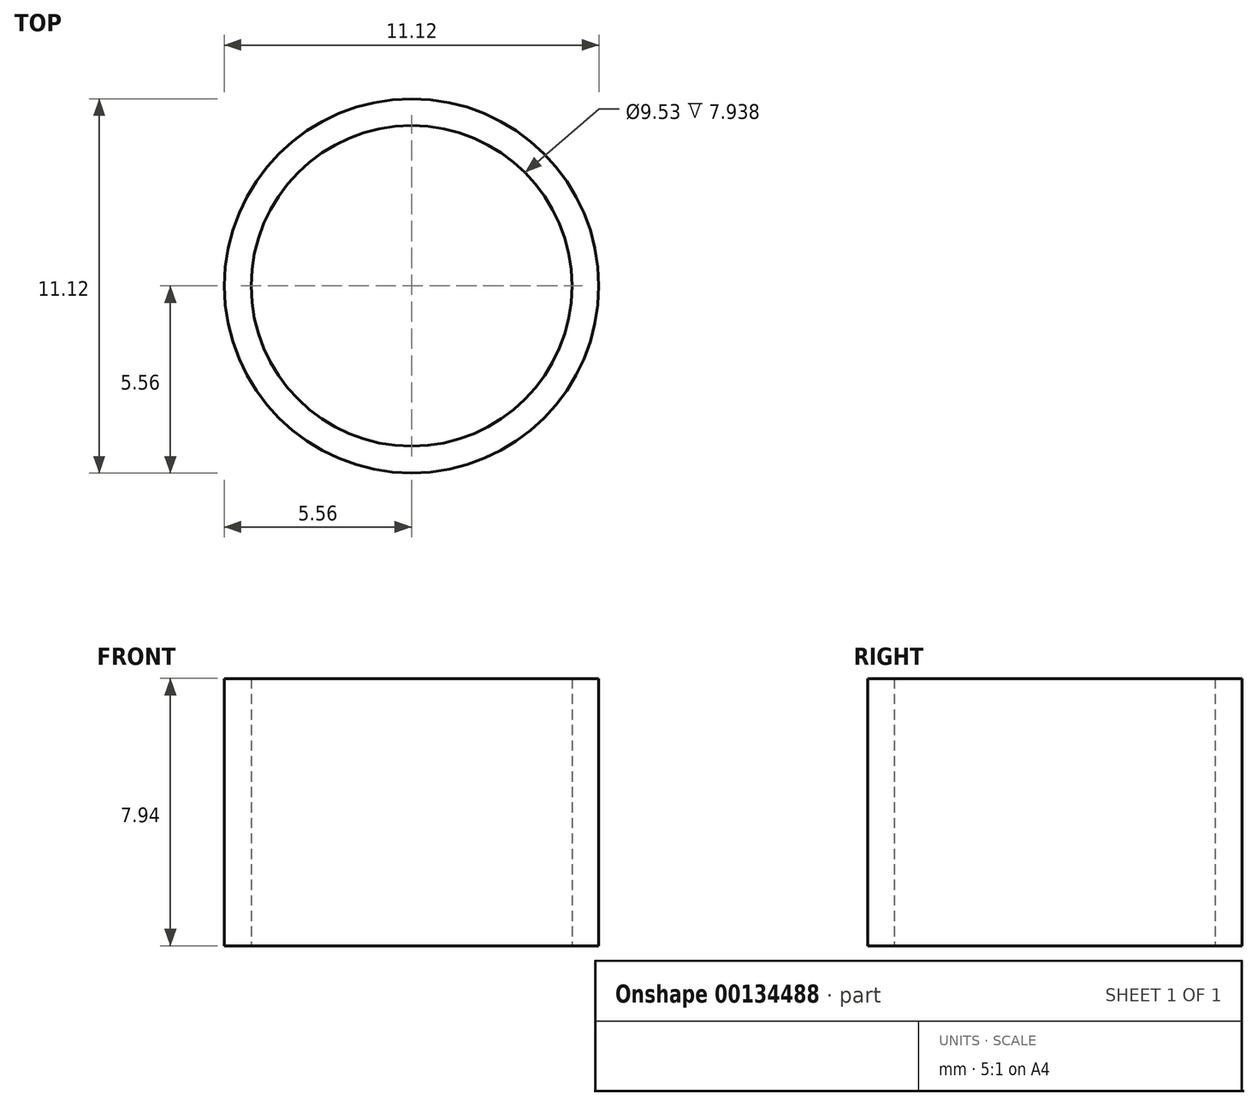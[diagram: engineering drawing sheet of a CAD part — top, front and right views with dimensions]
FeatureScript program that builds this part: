
annotation { "Feature Type Name" : "Feature", "Feature Type Description" : "" }
export const myFeature = defineFeature(function(context is Context, id is Id, definition is map)
    precondition{}
    {
        {
            var Q0;
            Q0=qCreatedBy(makeId("Top.planeOp"),FACE);
            var sketch = newSketch(context, id + "F0", { "sketchPlane" : qUnion([Q0])});
            skCircle(sketch, "E0", {"center": v(0, 0) * mm, "radius": 5.56 * mm});
            skCircle(sketch, "E1", {"center": v(0, 0) * mm, "radius": 4.76 * mm});
            skSolve(sketch);
        }
        {
            var Q0;
            Q0 = qSketchRegion(id + "F0", true);
            extrude(context, id + "F1", {"entities" : qUnion([Q0]), "depth" : 7.94 * mm});
        }
    });
